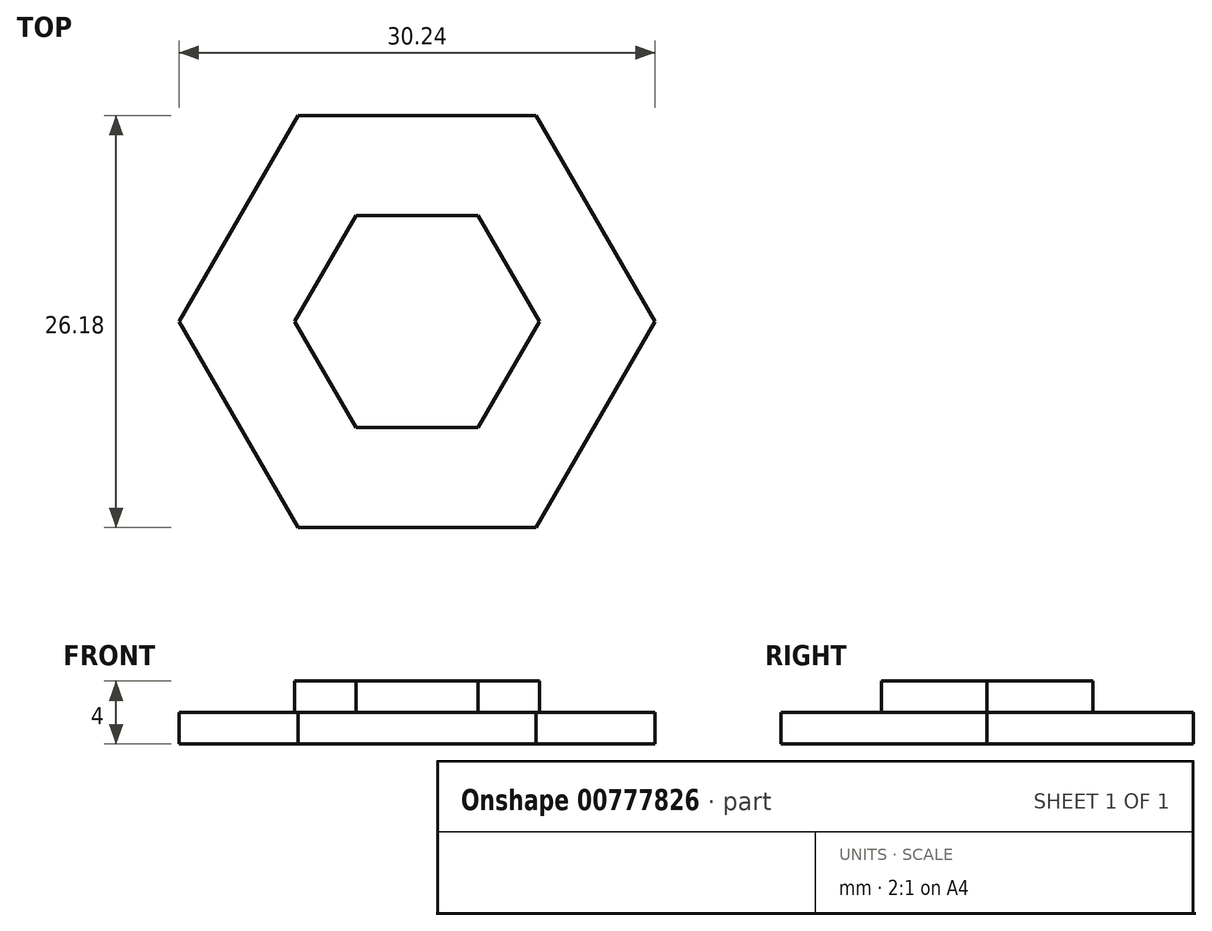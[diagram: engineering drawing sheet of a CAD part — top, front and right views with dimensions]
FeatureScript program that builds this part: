
annotation { "Feature Type Name" : "Feature", "Feature Type Description" : "" }
export const myFeature = defineFeature(function(context is Context, id is Id, definition is map)
    precondition{}
    {
        {
            var Q0;
            Q0=qCreatedBy(makeId("Top.planeOp"),FACE);
            var sketch = newSketch(context, id + "F0", { "sketchPlane" : qUnion([Q0])});
            skCircle(sketch, "E0.cCircle", {"center": v(0, 0) * mm, "radius": 13.1 * mm, "construction": true});
            skLineSegment(sketch, "E0.0", {"start": v(-7.56, 13.1) * mm, "end": v(7.56, 13.1) * mm});
            skLineSegment(sketch, "E0.1", {"start": v(7.56, 13.1) * mm, "end": v(15.12, 0) * mm});
            skLineSegment(sketch, "E0.2", {"start": v(15.12, 0) * mm, "end": v(7.56, -13.1) * mm});
            skLineSegment(sketch, "E0.3", {"start": v(7.56, -13.1) * mm, "end": v(-7.56, -13.1) * mm});
            skLineSegment(sketch, "E0.4", {"start": v(-7.56, -13.1) * mm, "end": v(-15.12, 0) * mm});
            skLineSegment(sketch, "E0.5", {"start": v(-15.12, 0) * mm, "end": v(-7.56, 13.1) * mm});
            skPoint(sketch, "E0.0.midPoint", {"position": v(0, 13.1) * mm});
            skSolve(sketch);
        }
        {
            var Q0;
            Q0=makeQuery(id+"F0.imprint","IMPRINT",FACE,{"disambiguationData":[TD([[makeQuery(id+"F0.imprint","IMPRINT",EDGE,{"derivedFrom":sQuery(id+"F0.wireOp",EDGE,"E0.0")}),-1.0]])]});
            extrude(context, id + "F1", {"entities" : qUnion([Q0]), "depth" : 2 * mm, "offsetDistance" : 25.4 * mm});
        }
        {
            var Q0;
            Q0=makeQuery(id+"F1.opExtrude","CAP_FACE",FACE,{"disambiguationData":[OSD([sQuery(id+"F0.wireOp",EDGE,"E0.0"),sQuery(id+"F0.wireOp",EDGE,"E0.1"),sQuery(id+"F0.wireOp",EDGE,"E0.2"),sQuery(id+"F0.wireOp",EDGE,"E0.3"),sQuery(id+"F0.wireOp",EDGE,"E0.4"),sQuery(id+"F0.wireOp",EDGE,"E0.5")])],"isStart":false});
            var sketch = newSketch(context, id + "F2", { "sketchPlane" : qUnion([Q0])});
            skCircle(sketch, "E1.cCircle", {"center": v(0, 0) * mm, "radius": 6.73 * mm, "construction": true});
            skLineSegment(sketch, "E1.0", {"start": v(-3.88, 6.73) * mm, "end": v(3.88, 6.73) * mm});
            skLineSegment(sketch, "E1.1", {"start": v(3.88, 6.73) * mm, "end": v(7.77, 0) * mm});
            skLineSegment(sketch, "E1.2", {"start": v(7.77, 0) * mm, "end": v(3.88, -6.73) * mm});
            skLineSegment(sketch, "E1.3", {"start": v(3.88, -6.73) * mm, "end": v(-3.88, -6.73) * mm});
            skLineSegment(sketch, "E1.4", {"start": v(-3.88, -6.73) * mm, "end": v(-7.77, 0) * mm});
            skLineSegment(sketch, "E1.5", {"start": v(-7.77, 0) * mm, "end": v(-3.88, 6.73) * mm});
            skPoint(sketch, "E1.0.midPoint", {"position": v(0, 6.73) * mm});
            skSolve(sketch);
        }
        {
            var Q0;
            Q0=makeQuery(id+"F2.imprint","IMPRINT",FACE,{"disambiguationData":[TD([[makeQuery(id+"F2.imprint","IMPRINT",EDGE,{"derivedFrom":sQuery(id+"F2.wireOp",EDGE,"E1.0")}),-1.0]])]});
            extrude(context, id + "F3", {"entities" : qUnion([Q0]), "operationType" : NewBodyOperationType.ADD, "depth" : 2 * mm, "offsetDistance" : 25.4 * mm});
        }
        {
            var Q0;
            Q0=makeQuery(id+"F1.opExtrude","CAP_FACE",FACE,{"disambiguationData":[OSD([sQuery(id+"F0.wireOp",EDGE,"E0.0"),sQuery(id+"F0.wireOp",EDGE,"E0.1"),sQuery(id+"F0.wireOp",EDGE,"E0.2"),sQuery(id+"F0.wireOp",EDGE,"E0.3"),sQuery(id+"F0.wireOp",EDGE,"E0.4"),sQuery(id+"F0.wireOp",EDGE,"E0.5")])],"isStart":true});
            var sketch = newSketch(context, id + "F4", { "sketchPlane" : qUnion([Q0])});
            skCircle(sketch, "E2", {"center": v(0, 13.1) * mm, "radius": 5.38 * mm});
            skCircle(sketch, "E3", {"center": v(0, 13.1) * mm, "radius": 2.94 * mm});
            skSolve(sketch);
        }
        {
            var Q0;
            Q0=sQuery(id+"F4.wireOp",EDGE,"E2");
            var Q1;
            Q1=sQuery(id+"F4.wireOp",EDGE,"E3");
            extrude(context, id + "F5", {"bodyType" : ToolBodyType.SURFACE, "surfaceEntities" : qUnion([Q0, Q1]), "oppositeDirection" : true, "depth" : 2 * mm, "offsetDistance" : 25.4 * mm});
        }
    });
